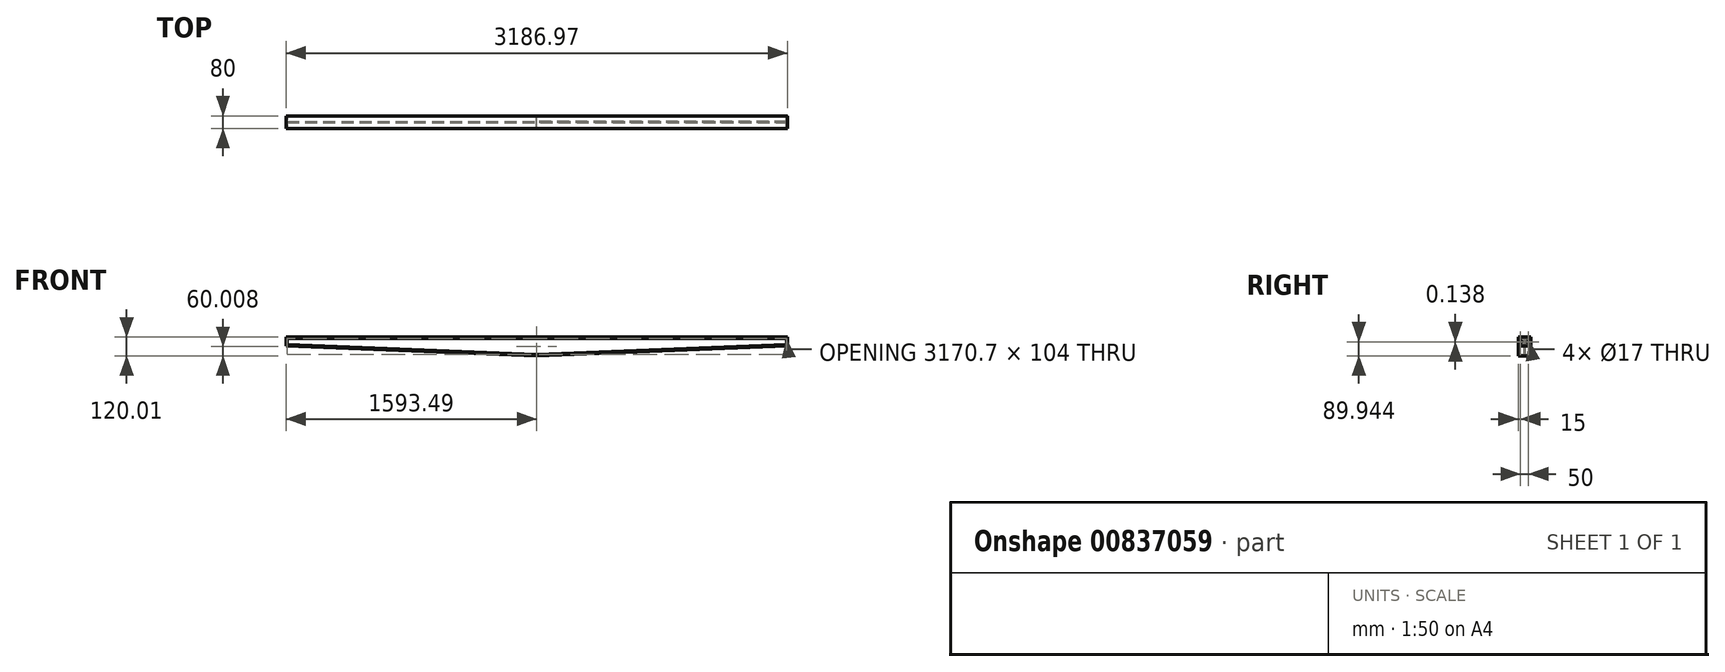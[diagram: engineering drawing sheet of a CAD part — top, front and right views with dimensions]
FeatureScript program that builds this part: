
annotation { "Feature Type Name" : "Feature", "Feature Type Description" : "" }
export const myFeature = defineFeature(function(context is Context, id is Id, definition is map)
    precondition{}
    {
        {
            var Q0;
            Q0=qCreatedBy(makeId("Front.planeOp"),FACE);
            var sketch = newSketch(context, id + "F0", { "sketchPlane" : qUnion([Q0])});
            skLineSegment(sketch, "E0", {"start": v(0, -32.95) * mm, "end": v(-1585, -32.95) * mm});
            skLineSegment(sketch, "E1", {"start": v(-1585, -32.95) * mm, "end": v(-1584.3, -72.95) * mm});
            skLineSegment(sketch, "E2", {"start": v(-1584.3, -72.95) * mm, "end": v(0, -136.95) * mm});
            skLineSegment(sketch, "E3.MirrorCS", {"start": v(0, -32.95) * mm, "end": v(1585, -32.95) * mm});
            skLineSegment(sketch, "E4", {"start": v(1585, -32.95) * mm, "end": v(1585.7, -72.95) * mm});
            skLineSegment(sketch, "E5", {"start": v(1585.7, -72.95) * mm, "end": v(0, -136.95) * mm});
            skSolve(sketch);
        }
        {
            var Q0;
            Q0=qSketchRegion(id+"F0",true);
            extrude(context, id + "F1", {"entities" : qUnion([Q0]), "depth" : 5 * mm, "offsetDistance" : 25 * mm, "symmetric" : true});
        }
        {
            var Q0;
            Q0=qCreatedBy(makeId("Front.planeOp"),FACE);
            var sketch = newSketch(context, id + "F2", { "sketchPlane" : qUnion([Q0])});
            skLineSegment(sketch, "E6", {"start": v(-1585, -32.95) * mm, "end": v(-1584.3, -72.95) * mm});
            skLineSegment(sketch, "E7", {"start": v(-1584.3, -72.95) * mm, "end": v(0, -136.95) * mm});
            skLineSegment(sketch, "E8", {"start": v(0, -136.95) * mm, "end": v(1585.7, -72.95) * mm});
            skLineSegment(sketch, "E9", {"start": v(1585.7, -72.95) * mm, "end": v(1585, -32.95) * mm});
            skLineSegment(sketch, "E10", {"start": v(1585, -32.95) * mm, "end": v(-1585, -32.95) * mm});
            skLineSegment(sketch, "E11", {"start": v(-1593.14, -24.95) * mm, "end": v(-1592.17, -80.63) * mm});
            skLineSegment(sketch, "E12", {"start": v(-1592.17, -80.63) * mm, "end": v(0, -144.96) * mm});
            skLineSegment(sketch, "E13", {"start": v(0, -144.96) * mm, "end": v(1593.83, -80.62) * mm});
            skLineSegment(sketch, "E14", {"start": v(1593.83, -80.62) * mm, "end": v(1592.86, -24.95) * mm});
            skLineSegment(sketch, "E15", {"start": v(1592.86, -24.95) * mm, "end": v(-1593.14, -24.95) * mm});
            skSolve(sketch);
        }
        {
            var Q0;
            Q0=qSketchRegion(id+"F2",true);
            extrude(context, id + "F3", {"entities" : qUnion([Q0]), "operationType" : NewBodyOperationType.ADD, "depth" : 80 * mm, "offsetDistance" : 25 * mm, "symmetric" : true});
        }
        {
            var Q0;
            Q0=makeQuery(id+"F3.opExtrude","SWEPT_FACE",FACE,{"disambiguationData":[OSD([sQuery(id+"F2.wireOp",EDGE,"E11")])]});
            var sketch = newSketch(context, id + "F4", { "sketchPlane" : qUnion([Q0])});
            skCircle(sketch, "E16", {"center": v(-25, -27.14) * mm, "radius": 8.5 * mm});
            skCircle(sketch, "E17.MirrorC", {"center": v(25, -27.14) * mm, "radius": 8.5 * mm});
            skSolve(sketch);
        }
        {
            var Q0;
            Q0 = qSketchRegion(id + "F4", true);
            extrude(context, id + "F5", {"entities" : qUnion([Q0]), "operationType" : NewBodyOperationType.REMOVE, "oppositeDirection" : true, "depth" : 25 * mm, "offsetDistance" : 25 * mm});
        }
        {
            var Q0;
            Q0=makeQuery(id+"F3.opExtrude","SWEPT_FACE",FACE,{"disambiguationData":[OSD([sQuery(id+"F2.wireOp",EDGE,"E14")])]});
            var sketch = newSketch(context, id + "F6", { "sketchPlane" : qUnion([Q0])});
            skCircle(sketch, "E18", {"center": v(-25, -82.75) * mm, "radius": 8.5 * mm});
            skCircle(sketch, "E19.MirrorC", {"center": v(25, -82.75) * mm, "radius": 8.5 * mm});
            skSolve(sketch);
        }
        {
            var Q0;
            Q0 = qSketchRegion(id + "F6", true);
            extrude(context, id + "F7", {"entities" : qUnion([Q0]), "operationType" : NewBodyOperationType.REMOVE, "oppositeDirection" : true, "depth" : 25 * mm, "offsetDistance" : 25 * mm});
        }
    });
